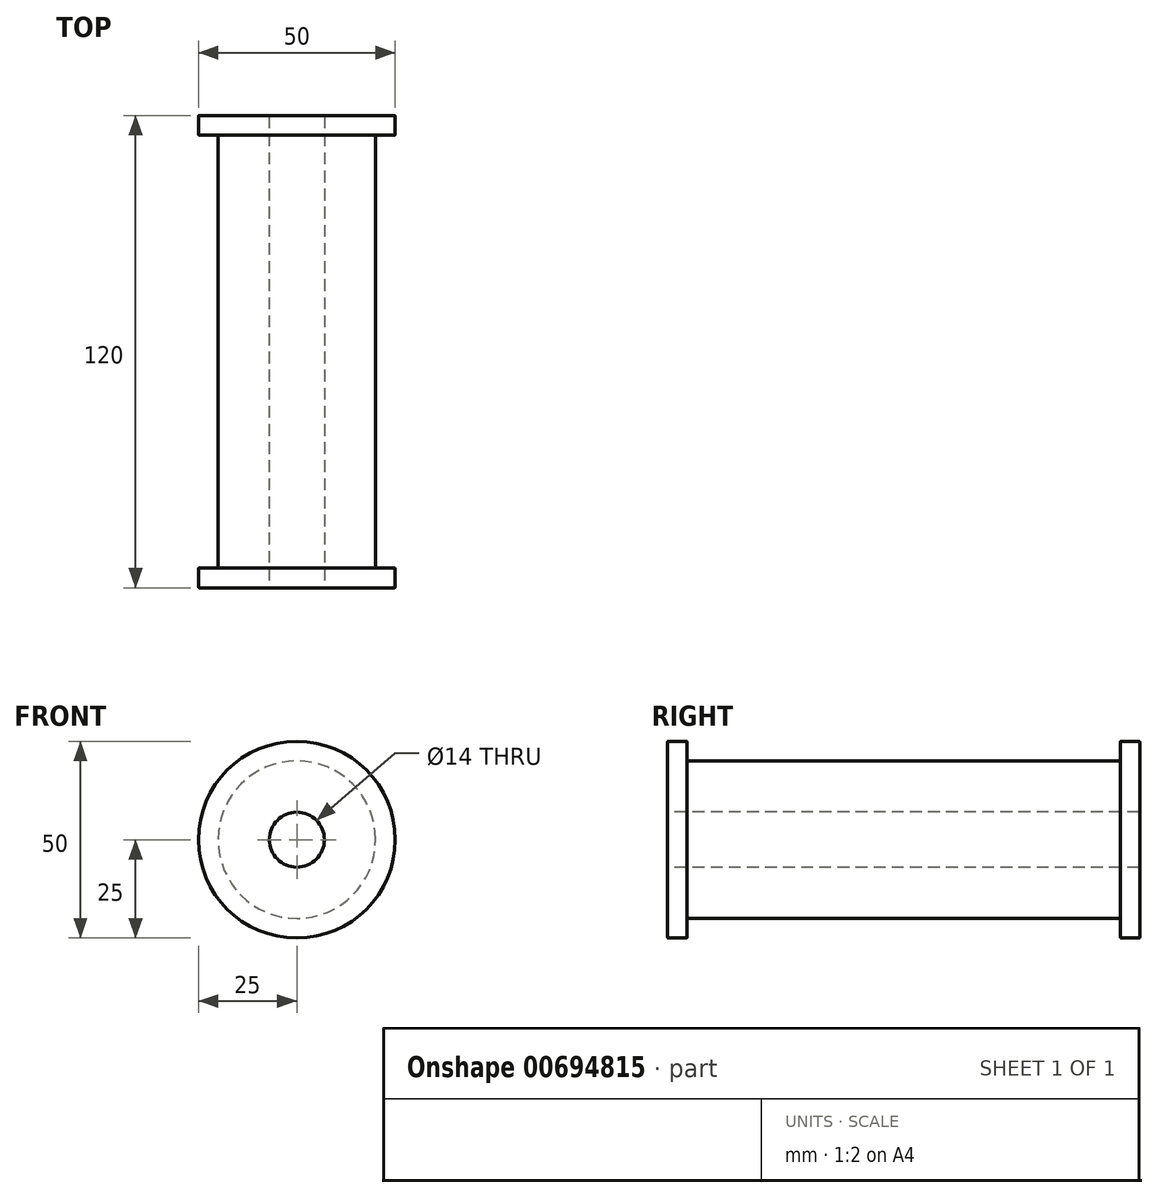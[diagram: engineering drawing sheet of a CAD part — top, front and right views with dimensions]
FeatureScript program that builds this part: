
annotation { "Feature Type Name" : "Feature", "Feature Type Description" : "" }
export const myFeature = defineFeature(function(context is Context, id is Id, definition is map)
    precondition{}
    {
        {
            var Q0;
            Q0=qCreatedBy(makeId("Front.planeOp"),FACE);
            var sketch = newSketch(context, id + "F0", { "sketchPlane" : qUnion([Q0])});
            skCircle(sketch, "E0", {"center": v(0, 0) * mm, "radius": 25 * mm});
            skSolve(sketch);
        }
        {
            var Q0;
            Q0=makeQuery(id+"F0.imprint","IMPRINT",FACE,{"disambiguationData":[TD([[makeQuery(id+"F0.imprint","IMPRINT",EDGE,{"derivedFrom":sQuery(id+"F0.wireOp",EDGE,"E0")}),1.0]])]});
            extrude(context, id + "F1", {"entities" : qUnion([Q0]), "depth" : 5 * mm, "offsetDistance" : 25 * mm});
        }
        {
            var Q0;
            Q0=makeQuery(id+"F1.opExtrude","CAP_FACE",FACE,{"disambiguationData":[OSD([sQuery(id+"F0.wireOp",EDGE,"E0")])],"isStart":false});
            var sketch = newSketch(context, id + "F2", { "sketchPlane" : qUnion([Q0])});
            skCircle(sketch, "E1", {"center": v(0, 0) * mm, "radius": 20 * mm});
            skSolve(sketch);
        }
        {
            var Q0;
            Q0=makeQuery(id+"F2.imprint","IMPRINT",FACE,{"disambiguationData":[TD([[makeQuery(id+"F2.imprint","IMPRINT",EDGE,{"derivedFrom":sQuery(id+"F2.wireOp",EDGE,"Z0M4IdSm-eEsB-ms9t-2QNI-JJkXDREfKQWJ")}),1.0]])]});
            var Q1;
            Q1=makeQuery(id+"F2.imprint","IMPRINT",FACE,{"disambiguationData":[TD([[makeQuery(id+"F2.imprint","IMPRINT",EDGE,{"derivedFrom":sQuery(id+"F2.wireOp",EDGE,"E1")}),1.0]])]});
            extrude(context, id + "F3", {"entities" : qUnion([Q0, Q1]), "operationType" : NewBodyOperationType.ADD, "depth" : 110 * mm, "offsetDistance" : 25 * mm});
        }
        {
            var Q0;
            Q0=makeQuery(id+"F3.opExtrude","CAP_FACE",FACE,{"disambiguationData":[OSD([sQuery(id+"F2.wireOp",EDGE,"E1")])],"isStart":false});
            var sketch = newSketch(context, id + "F4", { "sketchPlane" : qUnion([Q0])});
            skSolve(sketch);
        }
        {
            var Q0;
            Q0=makeQuery(id+"F4.imprint","IMPRINT",FACE,{"disambiguationData":[TD([[makeQuery(id+"F4.imprint","IMPRINT",EDGE,{"derivedFrom":makeQuery(id+"F3.opExtrude","CAP_EDGE",EDGE,{"disambiguationData":[OSD([sQuery(id+"F2.wireOp",EDGE,"E1")])],"isStart":false})}),1.0]])]});
            var sketch = newSketch(context, id + "F5", { "sketchPlane" : qUnion([Q0])});
            skCircle(sketch, "E2", {"center": v(0, 0) * mm, "radius": 25 * mm});
            skSolve(sketch);
        }
        {
            var Q0;
            Q0 = qSketchRegion(id + "F5", true);
            var Q1;
            Q1=makeQuery(id+"F4.imprint","IMPRINT",FACE,{"disambiguationData":[TD([[makeQuery(id+"F4.imprint","IMPRINT",EDGE,{"derivedFrom":makeQuery(id+"F3.opExtrude","CAP_EDGE",EDGE,{"disambiguationData":[OSD([sQuery(id+"F2.wireOp",EDGE,"E1")])],"isStart":false})}),1.0]])]});
            extrude(context, id + "F6", {"entities" : qUnion([Q0, Q1]), "operationType" : NewBodyOperationType.ADD, "depth" : 5 * mm, "offsetDistance" : 25 * mm});
        }
        {
            var Q0;
            Q0=makeQuery(id+"F6.boolean.opBoolean","MERGE",FACE,{"derivedFrom":[makeQuery(id+"F6.opExtrude","CAP_FACE",FACE,{"disambiguationData":[OSD([sQuery(id+"F2.wireOp",EDGE,"E1")])],"isStart":false}),makeQuery(id+"F6.opExtrude","CAP_FACE",FACE,{"disambiguationData":[OSD([sQuery(id+"F5.wireOp",EDGE,"E2")])],"isStart":false})]});
            var sketch = newSketch(context, id + "F7", { "sketchPlane" : qUnion([Q0])});
            skCircle(sketch, "E3", {"center": v(0, 0) * mm, "radius": 7 * mm});
            skSolve(sketch);
        }
        {
            var Q0;
            Q0=makeQuery(id+"F7.imprint","IMPRINT",FACE,{"disambiguationData":[TD([[makeQuery(id+"F7.imprint","IMPRINT",EDGE,{"derivedFrom":sQuery(id+"F7.wireOp",EDGE,"E3")}),1.0]])]});
            extrude(context, id + "F8", {"entities" : qUnion([Q0]), "operationType" : NewBodyOperationType.REMOVE, "oppositeDirection" : true, "depth" : 200 * mm, "offsetDistance" : 25 * mm});
        }
        {
            var Q0;
            Q0=makeQuery(id+"F6.opExtrude","CAP_EDGE",EDGE,{"disambiguationData":[OSD([sQuery(id+"F5.wireOp",EDGE,"E2")])],"isStart":false});
            var Q1;
            Q1=makeQuery(id+"F8.boolean.opBoolean","COPY",EDGE,{"derivedFrom":makeQuery(id+"F8.opExtrude","CAP_EDGE",EDGE,{"disambiguationData":[OSD([sQuery(id+"F7.wireOp",EDGE,"E3")])],"isStart":true})});
            var Q2;
            Q2=makeQuery(id+"F6.opExtrude","CAP_EDGE",EDGE,{"disambiguationData":[OSD([sQuery(id+"F5.wireOp",EDGE,"E2")])],"isStart":true});
            var Q3;
            Q3=makeQuery(id+"F1.opExtrude","CAP_EDGE",EDGE,{"disambiguationData":[OSD([sQuery(id+"F0.wireOp",EDGE,"E0")])],"isStart":false});
            var Q4;
            Q4=makeQuery(id+"F1.opExtrude","CAP_EDGE",EDGE,{"disambiguationData":[OSD([sQuery(id+"F0.wireOp",EDGE,"E0")])],"isStart":true});
            var Q5;
            Q5=makeQuery(id+"F8.boolean.opBoolean","INTERSECT",EDGE,{"derivedFrom":[makeQuery(id+"F1.opExtrude","CAP_FACE",FACE,{"disambiguationData":[OSD([sQuery(id+"F0.wireOp",EDGE,"E0")])],"isStart":true}),makeQuery(id+"F8.opExtrude","SWEPT_FACE",FACE,{"disambiguationData":[OSD([sQuery(id+"F7.wireOp",EDGE,"E3")])]})]});
            fillet(context, id + "F9", {"entities" : qUnion([Q0, Q1, Q2, Q3, Q4, Q5]), "radius" : .2 * mm, "tangentPropagation" : true, "allowEdgeOverflow" : false});
        }
    });
